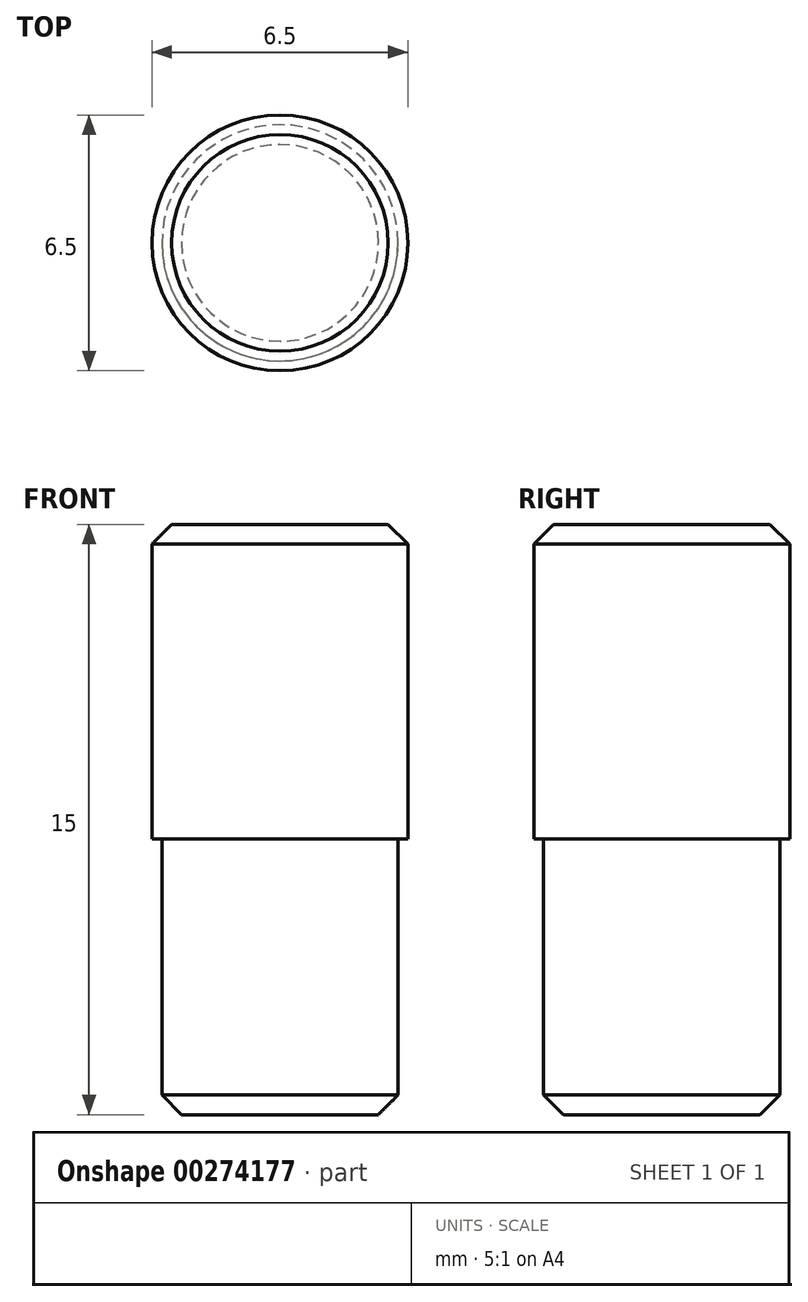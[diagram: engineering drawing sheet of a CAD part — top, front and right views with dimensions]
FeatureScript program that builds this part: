
annotation { "Feature Type Name" : "Feature", "Feature Type Description" : "" }
export const myFeature = defineFeature(function(context is Context, id is Id, definition is map)
    precondition{}
    {
        {
            var Q0;
            Q0=qCreatedBy(makeId("Front.planeOp"),FACE);
            var sketch = newSketch(context, id + "F0", { "sketchPlane" : qUnion([Q0])});
            skLineSegment(sketch, "E0", {"start": v(0, 0) * mm, "end": v(0, 8) * mm});
            skLineSegment(sketch, "E1", {"start": v(0, 8) * mm, "end": v(-3.25, 8) * mm});
            skLineSegment(sketch, "E2", {"start": v(-3.25, 8) * mm, "end": v(-3.25, 0) * mm});
            skLineSegment(sketch, "E3", {"start": v(-3.25, 0) * mm, "end": v(-3, 0) * mm});
            skLineSegment(sketch, "E4", {"start": v(-3, 0) * mm, "end": v(-3, -7) * mm});
            skLineSegment(sketch, "E5", {"start": v(-3, -7) * mm, "end": v(0, -7) * mm});
            skLineSegment(sketch, "E6", {"start": v(0, -7) * mm, "end": v(0, 0) * mm});
            skSolve(sketch);
        }
        {
            var Q0;
            Q0=makeQuery(id+"F0.imprint","IMPRINT",FACE,{"disambiguationData":[TD([[makeQuery(id+"F0.imprint","IMPRINT",EDGE,{"derivedFrom":sQuery(id+"F0.wireOp",EDGE,"E0")}),1.0]])]});
            var Q1;
            Q1=sQuery(id+"F0.wireOp",EDGE,"E0");
            revolve(context, id + "F1", {"entities" : qUnion([Q0]), "axis" : qUnion([Q1]), "revolveType" : RevolveType.FULL});
        }
        {
            var Q0;
            Q0=makeQuery(id+"F1.opRevolve","SWEPT_EDGE",EDGE,{"disambiguationData":[OSD([sQuery(id+"F0.wireOp",EDGE,"E1"),sQuery(id+"F0.wireOp",EDGE,"E2")])]});
            chamfer(context, id + "F2", {"entities" : qUnion([Q0]), "width" : 0.5 * mm, "tangentPropagation" : true});
        }
        {
            var Q0;
            Q0=makeQuery(id+"F1.opRevolve","SWEPT_EDGE",EDGE,{"disambiguationData":[OSD([sQuery(id+"F0.wireOp",EDGE,"E4"),sQuery(id+"F0.wireOp",EDGE,"E5")])]});
            chamfer(context, id + "F3", {"entities" : qUnion([Q0]), "width" : 0.5 * mm, "tangentPropagation" : true});
        }
    });
